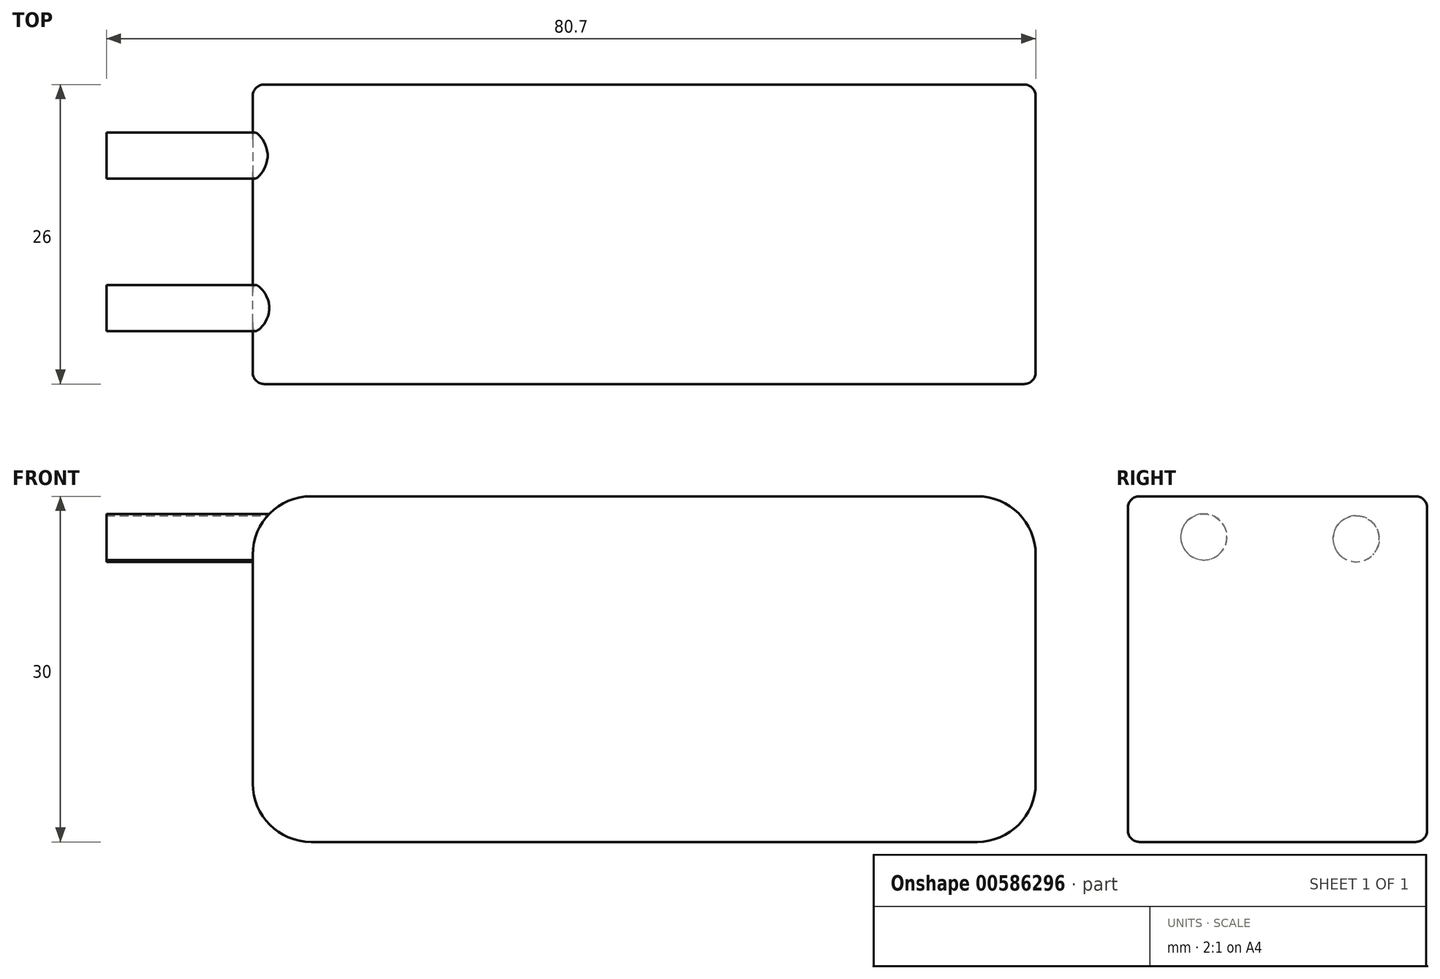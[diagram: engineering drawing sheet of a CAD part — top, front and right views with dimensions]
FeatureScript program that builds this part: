
annotation { "Feature Type Name" : "Feature", "Feature Type Description" : "" }
export const myFeature = defineFeature(function(context is Context, id is Id, definition is map)
    precondition{}
    {
        {
            var Q0;
            Q0=qCreatedBy(makeId("Front.planeOp"),FACE);
            var sketch = newSketch(context, id + "F0", { "sketchPlane" : qUnion([Q0])});
            skLineSegment(sketch, "E0.bottom", {"start": v(-9.3, 20.9) * mm, "end": v(58.7, 20.9) * mm});
            skLineSegment(sketch, "E0.top", {"start": v(-9.3, -9.1) * mm, "end": v(58.7, -9.1) * mm});
            skLineSegment(sketch, "E0.left", {"start": v(-9.3, 20.9) * mm, "end": v(-9.3, -9.1) * mm});
            skLineSegment(sketch, "E0.right", {"start": v(58.7, 20.9) * mm, "end": v(58.7, -9.1) * mm});
            skSolve(sketch);
        }
        {
            var Q0;
            Q0=makeQuery(id+"F0.imprint","IMPRINT",FACE,{"disambiguationData":[TD([[makeQuery(id+"F0.imprint","IMPRINT",EDGE,{"derivedFrom":sQuery(id+"F0.wireOp",EDGE,"E0.bottom")}),-1.0]])]});
            extrude(context, id + "F1", {"entities" : qUnion([Q0]), "depth" : 26 * mm, "offsetDistance" : 25.4 * mm});
        }
        {
            var Q0;
            Q0=makeQuery(id+"F1.opExtrude","SWEPT_FACE",FACE,{"disambiguationData":[OSD([sQuery(id+"F0.wireOp",EDGE,"E0.left")])]});
            var sketch = newSketch(context, id + "F2", { "sketchPlane" : qUnion([Q0])});
            skCircle(sketch, "E1", {"center": v(6.17, 17.2) * mm, "radius": 2 * mm});
            skCircle(sketch, "E2", {"center": v(19.4, 17.37) * mm, "radius": 2 * mm});
            skSolve(sketch);
        }
        {
            var Q0;
            Q0=makeQuery(id+"F2.imprint","IMPRINT",FACE,{"disambiguationData":[TD([[makeQuery(id+"F2.imprint","IMPRINT",EDGE,{"derivedFrom":sQuery(id+"F2.wireOp",EDGE,"E1")}),1.0]])]});
            var Q1;
            Q1=makeQuery(id+"F2.imprint","IMPRINT",FACE,{"disambiguationData":[TD([[makeQuery(id+"F2.imprint","IMPRINT",EDGE,{"derivedFrom":sQuery(id+"F2.wireOp",EDGE,"E2")}),1.0]])]});
            extrude(context, id + "F3", {"entities" : qUnion([Q0, Q1]), "operationType" : NewBodyOperationType.ADD, "depth" : 25.4 * mm, "offsetDistance" : 25.4 * mm});
        }
        {
            var Q0;
            Q0=makeQuery(id+"F1.opExtrude","SWEPT_EDGE",EDGE,{"disambiguationData":[OSD([sQuery(id+"F0.wireOp",EDGE,"E0.bottom"),sQuery(id+"F0.wireOp",EDGE,"E0.left")])]});
            var Q1;
            Q1=makeQuery(id+"F1.opExtrude","SWEPT_EDGE",EDGE,{"disambiguationData":[OSD([sQuery(id+"F0.wireOp",EDGE,"E0.bottom"),sQuery(id+"F0.wireOp",EDGE,"E0.right")])]});
            var Q2;
            Q2=makeQuery(id+"F1.opExtrude","SWEPT_EDGE",EDGE,{"disambiguationData":[OSD([sQuery(id+"F0.wireOp",EDGE,"E0.top"),sQuery(id+"F0.wireOp",EDGE,"E0.right")])]});
            var Q3;
            Q3=makeQuery(id+"F1.opExtrude","SWEPT_EDGE",EDGE,{"disambiguationData":[OSD([sQuery(id+"F0.wireOp",EDGE,"E0.top"),sQuery(id+"F0.wireOp",EDGE,"E0.left")])]});
            fillet(context, id + "F4", {"entities" : qUnion([Q0, Q1, Q2, Q3]), "radius" : 5.08 * mm, "tangentPropagation" : true, "allowEdgeOverflow" : false});
        }
        {
            var Q0;
            Q0=makeQuery(id+"F1.opExtrude","CAP_EDGE",EDGE,{"disambiguationData":[OSD([sQuery(id+"F0.wireOp",EDGE,"E0.top")])],"isStart":false});
            var Q1;
            Q1=makeQuery(id+"F1.opExtrude","CAP_EDGE",EDGE,{"disambiguationData":[OSD([sQuery(id+"F0.wireOp",EDGE,"E0.bottom")])],"isStart":false});
            var Q2;
            Q2=makeQuery(id+"F1.opExtrude","CAP_EDGE",EDGE,{"disambiguationData":[OSD([sQuery(id+"F0.wireOp",EDGE,"E0.left")])],"isStart":false});
            var Q3;
            Q3=makeQuery(id+"F1.opExtrude","CAP_EDGE",EDGE,{"disambiguationData":[OSD([sQuery(id+"F0.wireOp",EDGE,"E0.left")])],"isStart":true});
            var Q4;
            Q4=makeQuery(id+"F1.opExtrude","CAP_EDGE",EDGE,{"disambiguationData":[OSD([sQuery(id+"F0.wireOp",EDGE,"E0.top")])],"isStart":true});
            var Q5;
            Q5=makeQuery(id+"F1.opExtrude","CAP_EDGE",EDGE,{"disambiguationData":[OSD([sQuery(id+"F0.wireOp",EDGE,"E0.bottom")])],"isStart":true});
            var Q6;
            Q6=makeQuery(id+"F1.opExtrude","CAP_EDGE",EDGE,{"disambiguationData":[OSD([sQuery(id+"F0.wireOp",EDGE,"E0.right")])],"isStart":true});
            var Q7;
            Q7=makeQuery(id+"F1.opExtrude","CAP_EDGE",EDGE,{"disambiguationData":[OSD([sQuery(id+"F0.wireOp",EDGE,"E0.right")])],"isStart":false});
            fillet(context, id + "F5", {"entities" : qUnion([Q0, Q1, Q2, Q3, Q4, Q5, Q6, Q7]), "radius" : 1 * mm, "tangentPropagation" : true, "allowEdgeOverflow" : false});
        }
        {
            var Q0;
            Q0=makeQuery(id+"F3.opExtrude","CAP_FACE",FACE,{"disambiguationData":[OSD([sQuery(id+"F2.wireOp",EDGE,"E2")])],"isStart":false});
            var Q1;
            Q1=makeQuery(id+"F3.opExtrude","CAP_FACE",FACE,{"disambiguationData":[OSD([sQuery(id+"F2.wireOp",EDGE,"E1")])],"isStart":false});
            extrude(context, id + "F6", {"entities" : qUnion([Q0, Q1]), "operationType" : NewBodyOperationType.REMOVE, "oppositeDirection" : true, "depth" : 12.7 * mm, "offsetDistance" : 25.4 * mm});
        }
    });
